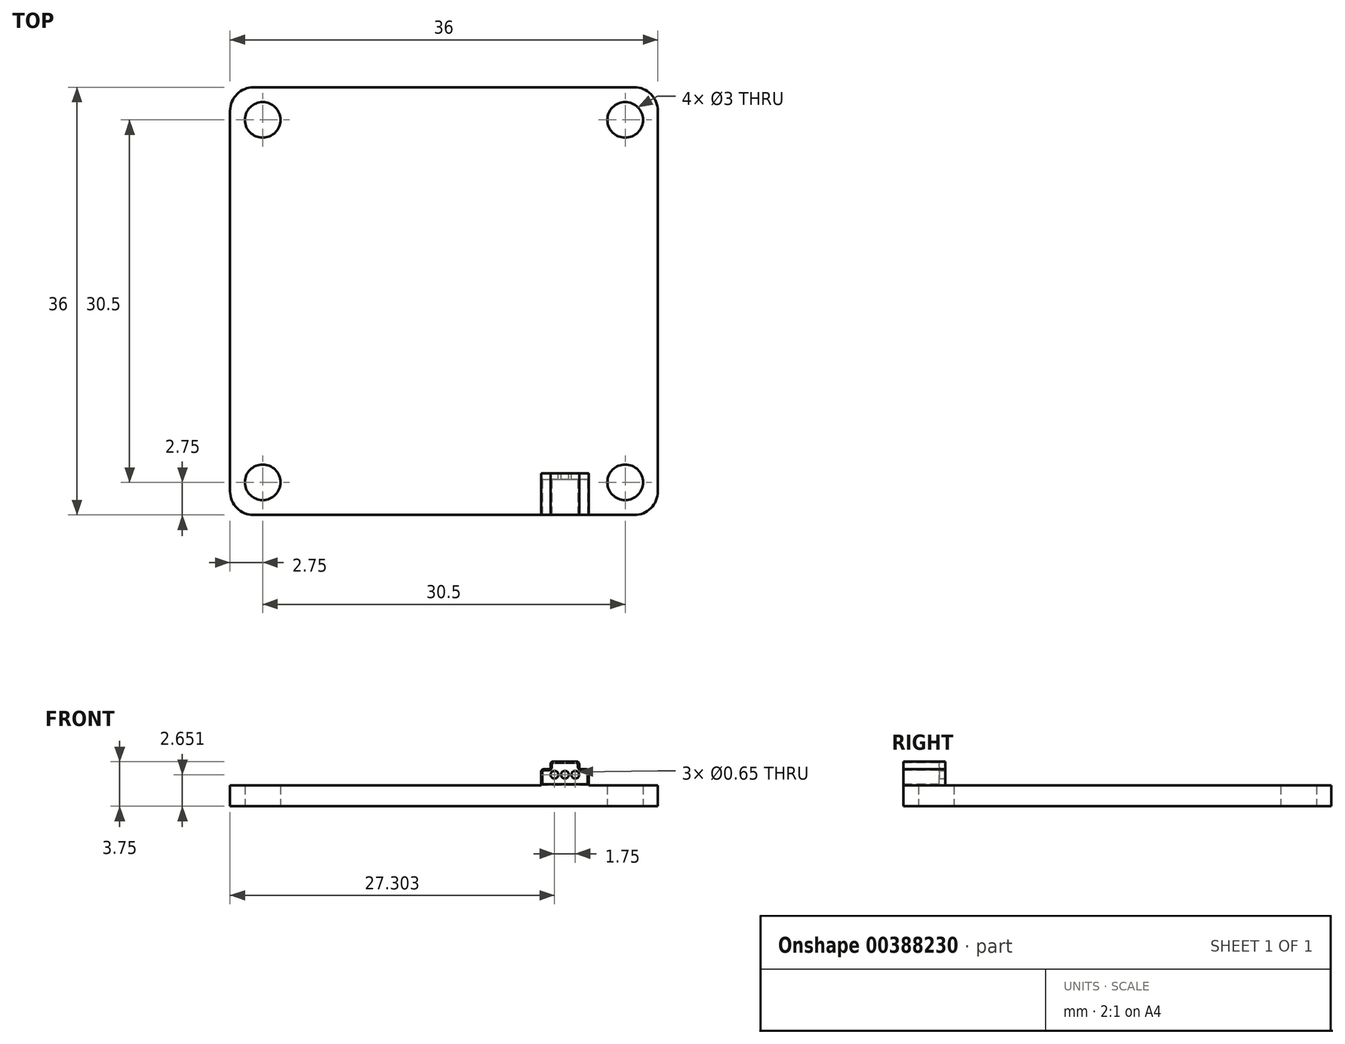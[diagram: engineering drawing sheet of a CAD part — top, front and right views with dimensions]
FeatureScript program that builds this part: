
annotation { "Feature Type Name" : "Feature", "Feature Type Description" : "" }
export const myFeature = defineFeature(function(context is Context, id is Id, definition is map)
    precondition{}
    {
        {
            var Q0;
            Q0=qCreatedBy(makeId("Top.planeOp"),FACE);
            var sketch = newSketch(context, id + "F0", { "sketchPlane" : qUnion([Q0])});
            skLineSegment(sketch, "E0.bottom", {"start": v(16, 18) * mm, "end": v(-16, 18) * mm});
            skLineSegment(sketch, "E0.top", {"start": v(16, -18) * mm, "end": v(-16, -18) * mm});
            skLineSegment(sketch, "E0.left", {"start": v(18, 16) * mm, "end": v(18, -16) * mm});
            skLineSegment(sketch, "E0.right", {"start": v(-18, 16) * mm, "end": v(-18, -16) * mm});
            skPoint(sketch, "E0.middle", {"position": v(0, 0) * mm});
            skLineSegment(sketch, "E1.bottom", {"start": v(15.25, 15.25) * mm, "end": v(-15.25, 15.25) * mm, "construction": true});
            skLineSegment(sketch, "E1.top", {"start": v(15.25, -15.25) * mm, "end": v(-15.25, -15.25) * mm, "construction": true});
            skLineSegment(sketch, "E1.left", {"start": v(15.25, 15.25) * mm, "end": v(15.25, -15.25) * mm, "construction": true});
            skLineSegment(sketch, "E1.right", {"start": v(-15.25, 15.25) * mm, "end": v(-15.25, -15.25) * mm, "construction": true});
            skCircle(sketch, "E2", {"center": v(-15.25, 15.25) * mm, "radius": 1.5 * mm});
            skCircle(sketch, "E3", {"center": v(15.25, 15.25) * mm, "radius": 1.5 * mm});
            skCircle(sketch, "E4", {"center": v(15.25, -15.25) * mm, "radius": 1.5 * mm});
            skCircle(sketch, "E5", {"center": v(-15.25, -15.25) * mm, "radius": 1.5 * mm});
            skPoint(sketch, "E6.visualSharp", {"position": v(-18, 18) * mm});
            skArc(sketch, "E6.filletArc", {"start": v(-16, 18) * mm, "mid": v(-17.41, 17.41) * mm, "end": v(-18, 16) * mm});
            skPoint(sketch, "E7.visualSharp", {"position": v(18, 18) * mm});
            skArc(sketch, "E7.filletArc", {"start": v(18, 16) * mm, "mid": v(17.41, 17.41) * mm, "end": v(16, 18) * mm});
            skPoint(sketch, "E8.visualSharp", {"position": v(18, -18) * mm});
            skArc(sketch, "E8.filletArc", {"start": v(16, -18) * mm, "mid": v(17.41, -17.41) * mm, "end": v(18, -16) * mm});
            skPoint(sketch, "E9.visualSharp", {"position": v(-18, -18) * mm});
            skArc(sketch, "E9.filletArc", {"start": v(-18, -16) * mm, "mid": v(-17.41, -17.41) * mm, "end": v(-16, -18) * mm});
            skSolve(sketch);
        }
        {
            var Q0;
            Q0=makeQuery(id+"F0.imprint","IMPRINT",FACE,{"disambiguationData":[TD([[makeQuery(id+"F0.imprint","IMPRINT",EDGE,{"derivedFrom":sQuery(id+"F0.wireOp",EDGE,"E0.bottom")}),1.0]])]});
            extrude(context, id + "F1", {"entities" : qUnion([Q0]), "depth" : 1.75 * mm});
        }
        {
            var Q0;
            Q0=makeQuery(id+"F1.opExtrude","SWEPT_FACE",FACE,{"disambiguationData":[OSD([sQuery(id+"F0.wireOp",EDGE,"E0.top")])]});
            var sketch = newSketch(context, id + "F2", { "sketchPlane" : qUnion([Q0])});
            skLineSegment(sketch, "E10.bottom", {"start": v(8.18, 1.75) * mm, "end": v(12.18, 1.75) * mm});
            skLineSegment(sketch, "E10.top", {"start": v(9.18, 3.75) * mm, "end": v(11.18, 3.75) * mm});
            skLineSegment(sketch, "E10.left", {"start": v(8.18, 1.75) * mm, "end": v(8.18, 2.9) * mm});
            skLineSegment(sketch, "E10.right", {"start": v(12.18, 1.75) * mm, "end": v(12.18, 2.9) * mm});
            skLineSegment(sketch, "E11", {"start": v(8.38, 3.1) * mm, "end": v(8.78, 3.1) * mm});
            skLineSegment(sketch, "E12", {"start": v(8.98, 3.3) * mm, "end": v(8.98, 3.55) * mm});
            skLineSegment(sketch, "E13", {"start": v(11.98, 3.1) * mm, "end": v(11.58, 3.1) * mm});
            skLineSegment(sketch, "E14", {"start": v(11.38, 3.3) * mm, "end": v(11.38, 3.55) * mm});
            skPoint(sketch, "E15.visualSharp", {"position": v(8.18, 3.1) * mm});
            skArc(sketch, "E15.filletArc", {"start": v(8.38, 3.1) * mm, "mid": v(8.24, 3.05) * mm, "end": v(8.18, 2.9) * mm});
            skPoint(sketch, "E16.visualSharp", {"position": v(8.98, 3.1) * mm});
            skArc(sketch, "E16.filletArc", {"start": v(8.78, 3.1) * mm, "mid": v(8.92, 3.17) * mm, "end": v(8.98, 3.3) * mm});
            skPoint(sketch, "E17.visualSharp", {"position": v(8.98, 3.75) * mm});
            skArc(sketch, "E17.filletArc", {"start": v(9.18, 3.75) * mm, "mid": v(9.04, 3.7) * mm, "end": v(8.98, 3.55) * mm});
            skPoint(sketch, "E18.visualSharp", {"position": v(11.38, 3.75) * mm});
            skArc(sketch, "E18.filletArc", {"start": v(11.38, 3.55) * mm, "mid": v(11.32, 3.7) * mm, "end": v(11.18, 3.75) * mm});
            skPoint(sketch, "E19.visualSharp", {"position": v(11.38, 3.1) * mm});
            skArc(sketch, "E19.filletArc", {"start": v(11.38, 3.3) * mm, "mid": v(11.44, 3.17) * mm, "end": v(11.58, 3.1) * mm});
            skPoint(sketch, "E20.visualSharp", {"position": v(12.18, 3.1) * mm});
            skArc(sketch, "E20.filletArc", {"start": v(12.18, 2.9) * mm, "mid": v(12.12, 3.05) * mm, "end": v(11.98, 3.1) * mm});
            skLineSegment(sketch, "E21.0", {"start": v(8.28, 1.85) * mm, "end": v(8.28, 2.9) * mm});
            skLineSegment(sketch, "E22.0", {"start": v(8.38, 3) * mm, "end": v(8.78, 3) * mm});
            skLineSegment(sketch, "E23.0", {"start": v(9.08, 3.3) * mm, "end": v(9.08, 3.55) * mm});
            skLineSegment(sketch, "E24.0", {"start": v(9.18, 3.65) * mm, "end": v(11.18, 3.65) * mm});
            skLineSegment(sketch, "E25.0", {"start": v(11.28, 3.3) * mm, "end": v(11.28, 3.55) * mm});
            skLineSegment(sketch, "E26.0", {"start": v(11.98, 3) * mm, "end": v(11.58, 3) * mm});
            skLineSegment(sketch, "E27.0", {"start": v(12.08, 1.85) * mm, "end": v(12.08, 2.9) * mm});
            skPoint(sketch, "E28.visualSharp", {"position": v(12.08, 3) * mm});
            skArc(sketch, "E28.filletArc", {"start": v(12.08, 2.9) * mm, "mid": v(12.05, 2.98) * mm, "end": v(11.98, 3) * mm});
            skPoint(sketch, "E29.visualSharp", {"position": v(11.28, 3) * mm});
            skArc(sketch, "E29.filletArc", {"start": v(11.28, 3.3) * mm, "mid": v(11.37, 3.1) * mm, "end": v(11.58, 3) * mm});
            skPoint(sketch, "E30.visualSharp", {"position": v(11.28, 3.65) * mm});
            skArc(sketch, "E30.filletArc", {"start": v(11.28, 3.55) * mm, "mid": v(11.25, 3.62) * mm, "end": v(11.18, 3.65) * mm});
            skPoint(sketch, "E31.visualSharp", {"position": v(9.08, 3.65) * mm});
            skArc(sketch, "E31.filletArc", {"start": v(9.18, 3.65) * mm, "mid": v(9.1, 3.62) * mm, "end": v(9.08, 3.55) * mm});
            skPoint(sketch, "E32.visualSharp", {"position": v(8.28, 3) * mm});
            skArc(sketch, "E32.filletArc", {"start": v(8.38, 3) * mm, "mid": v(8.3, 2.98) * mm, "end": v(8.28, 2.9) * mm});
            skPoint(sketch, "E33.visualSharp", {"position": v(9.08, 3) * mm});
            skArc(sketch, "E33.filletArc", {"start": v(8.78, 3) * mm, "mid": v(9, 3.1) * mm, "end": v(9.08, 3.3) * mm});
            skLineSegment(sketch, "E34", {"start": v(8.28, 1.85) * mm, "end": v(12.08, 1.85) * mm});
            skSolve(sketch);
        }
        {
            var Q0;
            Q0=makeQuery(id+"F2.imprint","IMPRINT",FACE,{"disambiguationData":[TD([[makeQuery(id+"F2.imprint","IMPRINT",EDGE,{"derivedFrom":sQuery(id+"F2.wireOp",EDGE,"E10.bottom")}),-1.0]])]});
            extrude(context, id + "F3", {"entities" : qUnion([Q0]), "operationType" : NewBodyOperationType.ADD, "oppositeDirection" : true, "depth" : 3 * mm});
        }
        {
            var Q0;
            Q0=makeQuery(id+"F3.opExtrude","CAP_FACE",FACE,{"disambiguationData":[OSD([sQuery(id+"F2.wireOp",EDGE,"E10.bottom"),sQuery(id+"F2.wireOp",EDGE,"E10.top"),sQuery(id+"F2.wireOp",EDGE,"E10.left"),sQuery(id+"F2.wireOp",EDGE,"E10.right"),sQuery(id+"F2.wireOp",EDGE,"E11"),sQuery(id+"F2.wireOp",EDGE,"E12"),sQuery(id+"F2.wireOp",EDGE,"E13"),sQuery(id+"F2.wireOp",EDGE,"E14"),sQuery(id+"F2.wireOp",EDGE,"E15.filletArc"),sQuery(id+"F2.wireOp",EDGE,"E16.filletArc"),sQuery(id+"F2.wireOp",EDGE,"E17.filletArc"),sQuery(id+"F2.wireOp",EDGE,"E18.filletArc"),sQuery(id+"F2.wireOp",EDGE,"E19.filletArc"),sQuery(id+"F2.wireOp",EDGE,"E20.filletArc"),sQuery(id+"F2.wireOp",EDGE,"E21.0"),sQuery(id+"F2.wireOp",EDGE,"E22.0"),sQuery(id+"F2.wireOp",EDGE,"E23.0"),sQuery(id+"F2.wireOp",EDGE,"E24.0"),sQuery(id+"F2.wireOp",EDGE,"E25.0"),sQuery(id+"F2.wireOp",EDGE,"E26.0"),sQuery(id+"F2.wireOp",EDGE,"E27.0"),sQuery(id+"F2.wireOp",EDGE,"E28.filletArc"),sQuery(id+"F2.wireOp",EDGE,"E29.filletArc"),sQuery(id+"F2.wireOp",EDGE,"E30.filletArc"),sQuery(id+"F2.wireOp",EDGE,"E31.filletArc"),sQuery(id+"F2.wireOp",EDGE,"E32.filletArc"),sQuery(id+"F2.wireOp",EDGE,"E33.filletArc"),sQuery(id+"F2.wireOp",EDGE,"E34")])],"isStart":false});
            var sketch = newSketch(context, id + "F4", { "sketchPlane" : qUnion([Q0])});
            skLineSegment(sketch, "E35.0", {"start": v(-8.18, 1.75) * mm, "end": v(-8.18, 2.9) * mm});
            skArc(sketch, "E36.0", {"start": v(-8.38, 3.1) * mm, "mid": v(-8.24, 3.05) * mm, "end": v(-8.18, 2.9) * mm});
            skLineSegment(sketch, "E37.0", {"start": v(-8.38, 3.1) * mm, "end": v(-8.78, 3.1) * mm});
            skArc(sketch, "E38.0", {"start": v(-8.78, 3.1) * mm, "mid": v(-8.92, 3.17) * mm, "end": v(-8.98, 3.3) * mm});
            skLineSegment(sketch, "E39.0", {"start": v(-8.98, 3.3) * mm, "end": v(-8.98, 3.55) * mm});
            skArc(sketch, "E40.0", {"start": v(-9.18, 3.75) * mm, "mid": v(-9.04, 3.7) * mm, "end": v(-8.98, 3.55) * mm});
            skLineSegment(sketch, "E41.0", {"start": v(-9.18, 3.75) * mm, "end": v(-11.18, 3.75) * mm});
            skLineSegment(sketch, "E42.0", {"start": v(-16, 1.75) * mm, "end": v(16, 1.75) * mm});
            skArc(sketch, "E43.0", {"start": v(-11.38, 3.55) * mm, "mid": v(-11.32, 3.7) * mm, "end": v(-11.18, 3.75) * mm});
            skLineSegment(sketch, "E44.0", {"start": v(-11.38, 3.3) * mm, "end": v(-11.38, 3.55) * mm});
            skArc(sketch, "E45.0", {"start": v(-11.38, 3.3) * mm, "mid": v(-11.44, 3.17) * mm, "end": v(-11.58, 3.1) * mm});
            skLineSegment(sketch, "E46.0", {"start": v(-11.98, 3.1) * mm, "end": v(-11.58, 3.1) * mm});
            skArc(sketch, "E47.0", {"start": v(-12.18, 2.9) * mm, "mid": v(-12.12, 3.05) * mm, "end": v(-11.98, 3.1) * mm});
            skLineSegment(sketch, "E48.0", {"start": v(-12.18, 1.75) * mm, "end": v(-12.18, 2.9) * mm});
            skSolve(sketch);
        }
        {
            var Q0;
            Q0=makeQuery(id+"F4.imprint","IMPRINT",FACE,{"disambiguationData":[TD([[makeQuery(id+"F4.imprint","IMPRINT",EDGE,{"derivedFrom":makeQuery(id+"F3.opExtrude","CAP_EDGE",EDGE,{"disambiguationData":[OSD([sQuery(id+"F2.wireOp",EDGE,"E21.0")])],"isStart":false})}),1.0]])]});
            var Q1;
            {var subQ1=sQuery(id+"F4.wireOp",EDGE,"E35.0");Q1=makeQuery(id+"F4.imprint","IMPRINT",FACE,{"disambiguationData":[TD([[makeQuery(id+"F4.imprint","IMPRINT",EDGE,{"derivedFrom":subQ1}),1.0]])]});}
            extrude(context, id + "F5", {"entities" : qUnion([Q0, Q1]), "operationType" : NewBodyOperationType.ADD, "depth" : .5 * mm});
        }
        {
            var Q0;
            Q0=makeQuery(id+"F5.opExtrude","CAP_FACE",FACE,{"disambiguationData":[OSD([sQuery(id+"F4.wireOp",EDGE,"E35.0"),sQuery(id+"F4.wireOp",EDGE,"E36.0"),sQuery(id+"F4.wireOp",EDGE,"E37.0"),sQuery(id+"F4.wireOp",EDGE,"E38.0"),sQuery(id+"F4.wireOp",EDGE,"E39.0"),sQuery(id+"F4.wireOp",EDGE,"E40.0"),sQuery(id+"F4.wireOp",EDGE,"E41.0"),sQuery(id+"F4.wireOp",EDGE,"E42.0"),sQuery(id+"F4.wireOp",EDGE,"E43.0"),sQuery(id+"F4.wireOp",EDGE,"E44.0"),sQuery(id+"F4.wireOp",EDGE,"E45.0"),sQuery(id+"F4.wireOp",EDGE,"E46.0"),sQuery(id+"F4.wireOp",EDGE,"E47.0"),sQuery(id+"F4.wireOp",EDGE,"E48.0")])],"isStart":false});
            var sketch = newSketch(context, id + "F6", { "sketchPlane" : qUnion([Q0])});
            skCircle(sketch, "E49", {"center": v(-11.05, 2.65) * mm, "radius": 0.33 * mm});
            skCircle(sketch, "E50", {"center": v(-10.18, 2.65) * mm, "radius": 0.33 * mm});
            skCircle(sketch, "E51", {"center": v(-9.3, 2.65) * mm, "radius": 0.33 * mm});
            skSolve(sketch);
        }
        {
            var Q0;
            Q0 = qSketchRegion(id + "F6", true);
            extrude(context, id + "F7", {"entities" : qUnion([Q0]), "operationType" : NewBodyOperationType.REMOVE, "oppositeDirection" : true, "depth" : 25 * mm});
        }
    });
